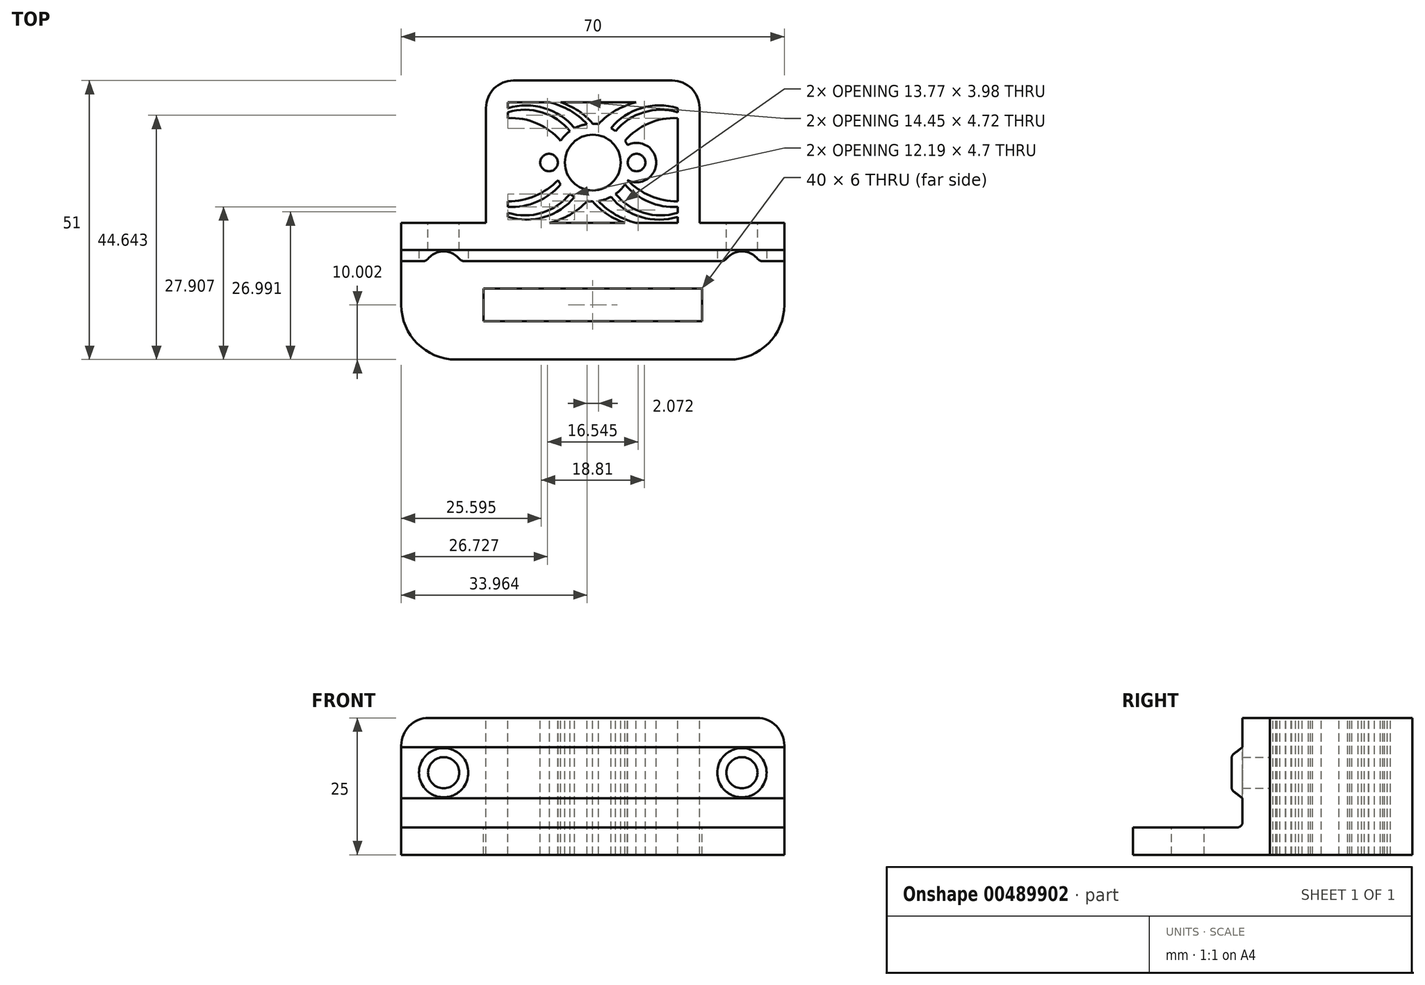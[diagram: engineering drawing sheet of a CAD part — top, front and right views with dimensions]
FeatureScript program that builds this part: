
annotation { "Feature Type Name" : "Feature", "Feature Type Description" : "" }
export const myFeature = defineFeature(function(context is Context, id is Id, definition is map)
    precondition{}
    {
        {
            var Q0;
            Q0=qCreatedBy(makeId("Top.planeOp"),FACE);
            var sketch = newSketch(context, id + "F0", { "sketchPlane" : qUnion([Q0])});
            skLineSegment(sketch, "E0.top", {"start": v(-40, -29.63) * mm, "end": v(0, -29.63) * mm});
            skLineSegment(sketch, "E0.left", {"start": v(-40, 0) * mm, "end": v(-40, -29.63) * mm});
            skLineSegment(sketch, "E0.right", {"start": v(0, 0) * mm, "end": v(0, -29.63) * mm});
            skPoint(sketch, "E1.oppositeSnap0", {"position": v(-20, -29.63) * mm});
            skLineSegment(sketch, "E2", {"start": v(-40, -9.63) * mm, "end": v(0, -9.63) * mm});
            skLineSegment(sketch, "E3", {"start": v(-20, -29.63) * mm, "end": v(-20, -9.63) * mm, "construction": true});
            skLineSegment(sketch, "E4.bottom", {"start": v(-55, -9.63) * mm, "end": v(15, -9.63) * mm});
            skLineSegment(sketch, "E4.top", {"start": v(-55, -4.63) * mm, "end": v(15, -4.63) * mm});
            skLineSegment(sketch, "E4.left", {"start": v(-55, -9.63) * mm, "end": v(-55, -4.63) * mm});
            skLineSegment(sketch, "E4.right", {"start": v(15, -9.63) * mm, "end": v(15, -4.63) * mm});
            skLineSegment(sketch, "E5", {"start": v(-55, -9.63) * mm, "end": v(-55, -19.63) * mm});
            skLineSegment(sketch, "E6", {"start": v(-45, -29.63) * mm, "end": v(-40, -29.63) * mm});
            skPoint(sketch, "E7.visualSharp", {"position": v(-55, -29.63) * mm});
            skArc(sketch, "E7.filletArc", {"start": v(-55, -19.63) * mm, "mid": v(-52.07, -26.7) * mm, "end": v(-45, -29.63) * mm});
            skLineSegment(sketch, "E8.MirrorCS", {"start": v(5, -29.63) * mm, "end": v(0, -29.63) * mm});
            skArc(sketch, "E9.MirrorCS", {"start": v(15, -19.63) * mm, "mid": v(12.07, -26.7) * mm, "end": v(5, -29.63) * mm});
            skLineSegment(sketch, "E10.MirrorCS", {"start": v(15, -9.63) * mm, "end": v(15, -19.63) * mm});
            skLineSegment(sketch, "E11.bottom", {"start": v(-40, -16.63) * mm, "end": v(0, -16.63) * mm});
            skLineSegment(sketch, "E11.top", {"start": v(-40, -22.63) * mm, "end": v(0, -22.63) * mm});
            skLineSegment(sketch, "E11.left", {"start": v(-40, -16.63) * mm, "end": v(-40, -22.63) * mm});
            skLineSegment(sketch, "E11.right", {"start": v(0, -16.63) * mm, "end": v(0, -22.63) * mm});
            skPoint(sketch, "E11.middle", {"position": v(-20, -19.63) * mm});
            skCircle(sketch, "E12", {"center": v(-20, 6.37) * mm, "radius": 5.1 * mm});
            skCircle(sketch, "E13", {"center": v(-28, 6.37) * mm, "radius": 1.6 * mm});
            skLineSegment(sketch, "E14", {"start": v(-20, 6.37) * mm, "end": v(-39.52, 6.37) * mm, "construction": true});
            skCircle(sketch, "E15.MirrorC", {"center": v(-12, 6.37) * mm, "radius": 1.6 * mm});
            skArc(sketch, "E16.0", {"start": v(-13.66, 9.57) * mm, "mid": v(-20, 13.47) * mm, "end": v(-26.34, 9.57) * mm});
            skArc(sketch, "E17.0", {"start": v(-26.34, 9.57) * mm, "mid": v(-31.6, 6.37) * mm, "end": v(-26.34, 3.18) * mm});
            skArc(sketch, "E18.0", {"start": v(-13.66, 9.57) * mm, "mid": v(-8.4, 6.37) * mm, "end": v(-13.66, 3.18) * mm});
            skArc(sketch, "E19.trimOffspring", {"start": v(-26.34, 3.18) * mm, "mid": v(-20, -0.73) * mm, "end": v(-13.66, 3.18) * mm});
            skLineSegment(sketch, "E20", {"start": v(-40, 0) * mm, "end": v(-40, 6.37) * mm});
            skLineSegment(sketch, "E21.MirrorCS", {"start": v(0, 0) * mm, "end": v(0, 6.37) * mm});
            skLineSegment(sketch, "E22.0", {"start": v(-35.5, -4.63) * mm, "end": v(-35.5, 17.37) * mm});
            skLineSegment(sketch, "E23.MirrorCS", {"start": v(-4.5, -4.63) * mm, "end": v(-4.5, 17.37) * mm});
            skLineSegment(sketch, "E24", {"start": v(-35.5, 17.37) * mm, "end": v(-4.5, 17.37) * mm});
            skArc(sketch, "E25", {"start": v(-18.95, 13.4) * mm, "mid": v(-15.82, 15.9) * mm, "end": v(-12.08, 17.37) * mm});
            skArc(sketch, "E26", {"start": v(-20, 13.47) * mm, "mid": v(-17.35, 15.83) * mm, "end": v(-14.15, 17.37) * mm});
            skArc(sketch, "E27.13.1", {"start": v(-14.11, 10.34) * mm, "mid": v(-9.8, 13.54) * mm, "end": v(-4.5, 14.48) * mm});
            skArc(sketch, "E27.14.0", {"start": v(-16.7, 12.65) * mm, "mid": v(-11.15, 16.33) * mm, "end": v(-4.5, 16.31) * mm});
            skArc(sketch, "E27.14.1", {"start": v(-13.66, 9.57) * mm, "mid": v(-9.48, 12.46) * mm, "end": v(-4.5, 13.48) * mm});
            skArc(sketch, "E27.15.0", {"start": v(-15.83, 12.12) * mm, "mid": v(-10.69, 15.57) * mm, "end": v(-4.5, 15.56) * mm});
            skPoint(sketch, "E28.trimOffspring.end.orphan", {"position": v(-6.09, 17.37) * mm});
            skLineSegment(sketch, "E29", {"start": v(-20, 6.37) * mm, "end": v(-20, -19.63) * mm, "construction": true});
            skArc(sketch, "E30.MirrorCS", {"start": v(-20, 13.47) * mm, "mid": v(-22.65, 15.83) * mm, "end": v(-25.85, 17.37) * mm});
            skArc(sketch, "E31.MirrorCS", {"start": v(-21.05, 13.4) * mm, "mid": v(-24.18, 15.9) * mm, "end": v(-27.92, 17.37) * mm});
            skArc(sketch, "E32.MirrorCS", {"start": v(-23.3, 12.65) * mm, "mid": v(-28.85, 16.33) * mm, "end": v(-35.5, 16.31) * mm});
            skArc(sketch, "E33.MirrorCS", {"start": v(-24.17, 12.12) * mm, "mid": v(-29.31, 15.57) * mm, "end": v(-35.5, 15.56) * mm});
            skArc(sketch, "E34.MirrorCS", {"start": v(-25.89, 10.34) * mm, "mid": v(-30.2, 13.54) * mm, "end": v(-35.5, 14.48) * mm});
            skArc(sketch, "E35.MirrorCS", {"start": v(-26.34, 9.57) * mm, "mid": v(-30.52, 12.46) * mm, "end": v(-35.5, 13.48) * mm});
            skArc(sketch, "E36.MirrorCS", {"start": v(-26.34, 3.18) * mm, "mid": v(-30.52, 0.28) * mm, "end": v(-35.5, -0.74) * mm});
            skArc(sketch, "E37.MirrorCS", {"start": v(-25.89, 2.4) * mm, "mid": v(-30.2, -0.8) * mm, "end": v(-35.5, -1.74) * mm});
            skArc(sketch, "E38.MirrorCS", {"start": v(-24.17, 0.63) * mm, "mid": v(-29.31, -2.82) * mm, "end": v(-35.5, -2.82) * mm});
            skArc(sketch, "E39.MirrorCS", {"start": v(-23.3, 0.1) * mm, "mid": v(-28.85, -3.59) * mm, "end": v(-35.5, -3.57) * mm});
            skArc(sketch, "E40.MirrorCS", {"start": v(-21.05, -0.65) * mm, "mid": v(-24.18, -3.16) * mm, "end": v(-27.92, -4.63) * mm});
            skArc(sketch, "E41.MirrorCS", {"start": v(-20, -0.73) * mm, "mid": v(-22.65, -3.09) * mm, "end": v(-25.85, -4.63) * mm});
            skArc(sketch, "E42.MirrorCS", {"start": v(-20, -0.73) * mm, "mid": v(-17.35, -3.09) * mm, "end": v(-14.15, -4.63) * mm});
            skArc(sketch, "E43.MirrorCS", {"start": v(-18.95, -0.65) * mm, "mid": v(-15.82, -3.16) * mm, "end": v(-12.08, -4.63) * mm});
            skArc(sketch, "E44.MirrorCS", {"start": v(-16.7, 0.1) * mm, "mid": v(-11.15, -3.59) * mm, "end": v(-4.5, -3.57) * mm});
            skArc(sketch, "E45.MirrorCS", {"start": v(-15.83, 0.63) * mm, "mid": v(-10.69, -2.82) * mm, "end": v(-4.5, -2.82) * mm});
            skArc(sketch, "E46.MirrorCS", {"start": v(-14.11, 2.4) * mm, "mid": v(-9.8, -0.8) * mm, "end": v(-4.5, -1.74) * mm});
            skArc(sketch, "E47.MirrorCS", {"start": v(-13.66, 3.18) * mm, "mid": v(-9.48, 0.28) * mm, "end": v(-4.5, -0.74) * mm});
            skLineSegment(sketch, "E48.0", {"start": v(-0.5, -4.63) * mm, "end": v(-0.5, 16.37) * mm});
            skLineSegment(sketch, "E48.1", {"start": v(-34.5, 21.37) * mm, "end": v(-5.5, 21.37) * mm});
            skLineSegment(sketch, "E48.2", {"start": v(-39.5, -4.63) * mm, "end": v(-39.5, 16.37) * mm});
            skPoint(sketch, "E49.visualSharp", {"position": v(-39.5, 21.37) * mm});
            skArc(sketch, "E49.filletArc", {"start": v(-34.5, 21.37) * mm, "mid": v(-38.04, 19.9) * mm, "end": v(-39.5, 16.37) * mm});
            skPoint(sketch, "E50.visualSharp", {"position": v(-0.5, 21.37) * mm});
            skArc(sketch, "E50.filletArc", {"start": v(-0.5, 16.37) * mm, "mid": v(-1.96, 19.9) * mm, "end": v(-5.5, 21.37) * mm});
            skSolve(sketch);
        }
        {
            var Q0;
            {var subQ5=sQuery(id+"F0.wireOp",EDGE,"E4.left");Q0=makeQuery(id+"F0.imprint","IMPRINT",FACE,{"disambiguationData":[TD([[makeQuery(id+"F0.imprint","IMPRINT",EDGE,{"derivedFrom":subQ5}),-1.0]])]});}
            var Q1;
            {var subQ5=sQuery(id+"F0.wireOp",EDGE,"E4.right");Q1=makeQuery(id+"F0.imprint","IMPRINT",FACE,{"disambiguationData":[TD([[makeQuery(id+"F0.imprint","IMPRINT",EDGE,{"derivedFrom":subQ5}),1.0]])]});}
            var Q2;
            {var subQ0=sQuery(id+"F0.wireOp",EDGE,"E0.top");Q2=makeQuery(id+"F0.imprint","IMPRINT",FACE,{"disambiguationData":[TD([[makeQuery(id+"F0.imprint","IMPRINT",EDGE,{"derivedFrom":subQ0}),1.0]])]});}
            var Q3;
            {var subQ2=sQuery(id+"F0.wireOp",EDGE,"E27.13.1");Q3=makeQuery(id+"F0.imprint","IMPRINT",FACE,{"disambiguationData":[TD([[makeQuery(id+"F0.imprint","IMPRINT",EDGE,{"derivedFrom":subQ2}),-1.0]])]});}
            var Q4;
            {var subQ0=sQuery(id+"F0.wireOp",EDGE,"E27.14.0");Q4=makeQuery(id+"F0.imprint","IMPRINT",FACE,{"disambiguationData":[TD([[makeQuery(id+"F0.imprint","IMPRINT",EDGE,{"derivedFrom":subQ0}),-1.0]])]});}
            var Q5;
            {var subQ0=sQuery(id+"F0.wireOp",EDGE,"E25");Q5=makeQuery(id+"F0.imprint","IMPRINT",FACE,{"disambiguationData":[TD([[makeQuery(id+"F0.imprint","IMPRINT",EDGE,{"derivedFrom":subQ0}),1.0]])]});}
            var Q6;
            {var subQ0=sQuery(id+"F0.wireOp",EDGE,"E30.MirrorCS");Q6=makeQuery(id+"F0.imprint","IMPRINT",FACE,{"disambiguationData":[TD([[makeQuery(id+"F0.imprint","IMPRINT",EDGE,{"derivedFrom":subQ0}),1.0]])]});}
            var Q7;
            {var subQ0=sQuery(id+"F0.wireOp",EDGE,"E32.MirrorCS");Q7=makeQuery(id+"F0.imprint","IMPRINT",FACE,{"disambiguationData":[TD([[makeQuery(id+"F0.imprint","IMPRINT",EDGE,{"derivedFrom":subQ0}),1.0]])]});}
            var Q8;
            {var subQ2=sQuery(id+"F0.wireOp",EDGE,"E34.MirrorCS");Q8=makeQuery(id+"F0.imprint","IMPRINT",FACE,{"disambiguationData":[TD([[makeQuery(id+"F0.imprint","IMPRINT",EDGE,{"derivedFrom":subQ2}),1.0]])]});}
            var Q9;
            {var subQ0=sQuery(id+"F0.wireOp",EDGE,"E36.MirrorCS");Q9=makeQuery(id+"F0.imprint","IMPRINT",FACE,{"disambiguationData":[TD([[makeQuery(id+"F0.imprint","IMPRINT",EDGE,{"derivedFrom":subQ0}),1.0]])]});}
            var Q10;
            {var subQ0=sQuery(id+"F0.wireOp",EDGE,"E38.MirrorCS");Q10=makeQuery(id+"F0.imprint","IMPRINT",FACE,{"disambiguationData":[TD([[makeQuery(id+"F0.imprint","IMPRINT",EDGE,{"derivedFrom":subQ0}),1.0]])]});}
            var Q11;
            {var subQ0=sQuery(id+"F0.wireOp",EDGE,"E44.MirrorCS");Q11=makeQuery(id+"F0.imprint","IMPRINT",FACE,{"disambiguationData":[TD([[makeQuery(id+"F0.imprint","IMPRINT",EDGE,{"derivedFrom":subQ0}),1.0]])]});}
            var Q12;
            {var subQ2=sQuery(id+"F0.wireOp",EDGE,"E46.MirrorCS");Q12=makeQuery(id+"F0.imprint","IMPRINT",FACE,{"disambiguationData":[TD([[makeQuery(id+"F0.imprint","IMPRINT",EDGE,{"derivedFrom":subQ2}),1.0]])]});}
            var Q13;
            {var subQ0=sQuery(id+"F0.wireOp",EDGE,"E5");Q13=makeQuery(id+"F0.imprint","IMPRINT",FACE,{"disambiguationData":[TD([[makeQuery(id+"F0.imprint","IMPRINT",EDGE,{"derivedFrom":subQ0}),1.0]])]});}
            var Q14;
            {var subQ0=sQuery(id+"F0.wireOp",EDGE,"E8.MirrorCS");Q14=makeQuery(id+"F0.imprint","IMPRINT",FACE,{"disambiguationData":[TD([[makeQuery(id+"F0.imprint","IMPRINT",EDGE,{"derivedFrom":subQ0}),-1.0]])]});}
            var Q15;
            {var subQ1=sQuery(id+"F0.wireOp",EDGE,"E0.left");var subQ5=sQuery(id+"F0.wireOp",EDGE,"E4.top");var subQ10=makeQuery(id+"F0.imprint","INTERSECT",VERTEX,{"derivedFrom":[subQ1,subQ5]});Q15=makeQuery(id+"F0.imprint","IMPRINT",FACE,{"disambiguationData":[TD([[makeQuery(id+"F0.imprint","IMPRINT",EDGE,{"disambiguationData":[TD([[subQ10,-1.0]])],"derivedFrom":subQ1}),1.0]])]});}
            var Q16;
            Q16=makeQuery(id+"F0.imprint","IMPRINT",FACE,{"disambiguationData":[TD([[makeQuery(id+"F0.imprint","IMPRINT",EDGE,{"derivedFrom":sQuery(id+"F0.wireOp",EDGE,"E12")}),-1.0]])]});
            var Q17;
            {var subQ0=sQuery(id+"F0.wireOp",EDGE,"E42.MirrorCS");Q17=makeQuery(id+"F0.imprint","IMPRINT",FACE,{"disambiguationData":[TD([[makeQuery(id+"F0.imprint","IMPRINT",EDGE,{"derivedFrom":subQ0}),1.0]])]});}
            var Q18;
            {var subQ0=sQuery(id+"F0.wireOp",EDGE,"E40.MirrorCS");Q18=makeQuery(id+"F0.imprint","IMPRINT",FACE,{"disambiguationData":[TD([[makeQuery(id+"F0.imprint","IMPRINT",EDGE,{"derivedFrom":subQ0}),1.0]])]});}
            var Q19;
            {var subQ24=sQuery(id+"F0.wireOp",EDGE,"E48.0");Q19=makeQuery(id+"F0.imprint","IMPRINT",FACE,{"disambiguationData":[TD([[makeQuery(id+"F0.imprint","IMPRINT",EDGE,{"derivedFrom":subQ24}),1.0]])]});}
            var Q20;
            {var subQ0=sQuery(id+"F0.wireOp",EDGE,"E11.bottom");Q20=makeQuery(id+"F0.imprint","IMPRINT",FACE,{"disambiguationData":[TD([[makeQuery(id+"F0.imprint","IMPRINT",EDGE,{"derivedFrom":subQ0}),1.0]])]});}
            extrude(context, id + "F1", {"entities" : qUnion([Q0, Q1, Q2, Q3, Q4, Q5, Q6, Q7, Q8, Q9, Q10, Q11, Q12, Q13, Q14, Q15, Q16, Q17, Q18, Q19, Q20]), "oppositeDirection" : true, "depth" : 25 * mm});
        }
        {
            var Q0;
            {var subQ1=sQuery(id+"F0.wireOp",EDGE,"E0.top");Q0=makeQuery(id+"F0.imprint","IMPRINT",FACE,{"disambiguationData":[TD([[makeQuery(id+"F0.imprint","IMPRINT",EDGE,{"derivedFrom":subQ1}),1.0]])]});}
            var Q1;
            {var subQ0=sQuery(id+"F0.wireOp",EDGE,"MP0E4fPa-GQLl-2h6X-QoBP-9llfqrqqr4Ud");Q1=makeQuery(id+"F0.imprint","IMPRINT",FACE,{"disambiguationData":[TD([[makeQuery(id+"F0.imprint","IMPRINT",EDGE,{"derivedFrom":subQ0}),-1.0]])]});}
            var Q2;
            {var subQ0=sQuery(id+"F0.wireOp",EDGE,"nStD9vQv-VlbH-pENE-0mBm-z8rxFK4uViPM");Q2=makeQuery(id+"F0.imprint","IMPRINT",FACE,{"disambiguationData":[TD([[makeQuery(id+"F0.imprint","IMPRINT",EDGE,{"derivedFrom":subQ0}),1.0]])]});}
            var Q3;
            {var subQ1=sQuery(id+"F0.wireOp",EDGE,"E5");Q3=makeQuery(id+"F0.imprint","IMPRINT",FACE,{"disambiguationData":[TD([[makeQuery(id+"F0.imprint","IMPRINT",EDGE,{"derivedFrom":subQ1}),1.0]])]});}
            var Q4;
            {var subQ0=sQuery(id+"F0.wireOp",EDGE,"E8.MirrorCS");Q4=makeQuery(id+"F0.imprint","IMPRINT",FACE,{"disambiguationData":[TD([[makeQuery(id+"F0.imprint","IMPRINT",EDGE,{"derivedFrom":subQ0}),-1.0]])]});}
            var Q5;
            {var subQ0=sQuery(id+"F0.wireOp",EDGE,"E11.bottom");Q5=makeQuery(id+"F0.imprint","IMPRINT",FACE,{"disambiguationData":[TD([[makeQuery(id+"F0.imprint","IMPRINT",EDGE,{"derivedFrom":subQ0}),1.0]])]});}
            extrude(context, id + "F2", {"entities" : qUnion([Q0, Q1, Q2, Q3, Q4, Q5]), "operationType" : NewBodyOperationType.REMOVE, "oppositeDirection" : true, "depth" : 20 * mm});
        }
        {
            var Q0;
            {var subQ0=sQuery(id+"F0.wireOp",EDGE,"E4.top");Q0=makeQuery(id+"F1.opExtrude","SWEPT_FACE",FACE,{"disambiguationData":[OSD([subQ0]),TDD([makeQuery(id+"F0.imprint","IMPRINT",EDGE,{"disambiguationData":[TD([[makeQuery(id+"F0.imprint","INTERSECT",VERTEX,{"derivedFrom":[subQ0,sQuery(id+"F0.wireOp",EDGE,"E4.left")]}),-1.0]])],"derivedFrom":subQ0})])]});}
            var sketch = newSketch(context, id + "F3", { "sketchPlane" : qUnion([Q0])});
            skCircle(sketch, "E51", {"center": v(47.25, -10) * mm, "radius": 2.85 * mm});
            skPoint(sketch, "E51.centerSnap0", {"position": v(47.25, 0) * mm});
            skPoint(sketch, "E51.centerSnap1", {"position": v(58, -10) * mm});
            skPoint(sketch, "E52.0", {"position": v(20, 0) * mm});
            skLineSegment(sketch, "E53", {"start": v(20, 0) * mm, "end": v(20, -39.52) * mm, "construction": true});
            skCircle(sketch, "E54.MirrorC", {"center": v(-7.25, -10) * mm, "radius": 2.85 * mm});
            skSolve(sketch);
        }
        {
            var Q0;
            Q0=makeQuery(id+"F1.opExtrude","SWEPT_FACE",FACE,{"disambiguationData":[OSD([sQuery(id+"F0.wireOp",EDGE,"E4.right"),sQuery(id+"F0.wireOp",EDGE,"E10.MirrorCS")])]});
            var sketch = newSketch(context, id + "F4", { "sketchPlane" : qUnion([Q0])});
            skLineSegment(sketch, "E55", {"start": v(-9.63, -10) * mm, "end": v(-13.18, -10) * mm, "construction": true});
            skLineSegment(sketch, "E56", {"start": v(-11.63, -10) * mm, "end": v(-11.63, -7.35) * mm});
            skLineSegment(sketch, "E57", {"start": v(-11.23, -6.55) * mm, "end": v(-9.63, -5.35) * mm});
            skLineSegment(sketch, "E58", {"start": v(-9.63, -5.35) * mm, "end": v(-9.63, -10) * mm});
            skPoint(sketch, "E59.visualSharp", {"position": v(-11.63, -6.85) * mm});
            skArc(sketch, "E59.filletArc", {"start": v(-11.23, -6.55) * mm, "mid": v(-11.52, -6.9) * mm, "end": v(-11.63, -7.35) * mm});
            skLineSegment(sketch, "E60.MirrorCS", {"start": v(-11.63, -10) * mm, "end": v(-11.63, -12.65) * mm});
            skArc(sketch, "E61.MirrorCS", {"start": v(-11.23, -13.45) * mm, "mid": v(-11.52, -13.1) * mm, "end": v(-11.63, -12.65) * mm});
            skLineSegment(sketch, "E62.MirrorCS", {"start": v(-11.23, -13.45) * mm, "end": v(-9.63, -14.65) * mm});
            skLineSegment(sketch, "E63.MirrorCS", {"start": v(-9.63, -14.65) * mm, "end": v(-9.63, -10) * mm});
            skSolve(sketch);
        }
        {
            var Q0;
            Q0=makeQuery(id+"F4.imprint","IMPRINT",FACE,{"disambiguationData":[TD([[makeQuery(id+"F4.imprint","IMPRINT",EDGE,{"derivedFrom":sQuery(id+"F4.wireOp",EDGE,"E56")}),-1.0]])]});
            var Q1;
            Q1=makeQuery(id+"F1.opExtrude","SWEPT_FACE",FACE,{"disambiguationData":[OSD([sQuery(id+"F0.wireOp",EDGE,"E4.left"),sQuery(id+"F0.wireOp",EDGE,"E5")])]});
            extrude(context, id + "F5", {"entities" : qUnion([Q0]), "operationType" : NewBodyOperationType.ADD, "endBound" : BoundingType.UP_TO_SURFACE, "oppositeDirection" : true, "endBoundEntityFace" : qUnion([Q1]), "depth" : 25 * mm});
        }
        {
            var Q0;
            Q0 = qSketchRegion(id + "F3", true);
            extrude(context, id + "F6", {"entities" : qUnion([Q0]), "operationType" : NewBodyOperationType.REMOVE, "endBound" : BoundingType.THROUGH_ALL, "oppositeDirection" : true, "depth" : 25 * mm});
        }
        {
            var Q0;
            Q0=makeQuery(id+"F6.boolean.opBoolean","SPLIT",FACE,{"disambiguationData":[TD([makeQuery(id+"F5.opExtrude","SWEPT_FACE",FACE,{"disambiguationData":[OSD([sQuery(id+"F4.wireOp",EDGE,"E59.filletArc")])]}),makeQuery(id+"F5.opExtrude","SWEPT_FACE",FACE,{"disambiguationData":[OSD([sQuery(id+"F4.wireOp",EDGE,"E61.MirrorCS")])]}),makeQuery(id+"F6.opExtrude","SWEPT_FACE",FACE,{"disambiguationData":[OSD([sQuery(id+"F3.wireOp",EDGE,"E51")])]}),makeQuery(id+"F6.opExtrude","SWEPT_FACE",FACE,{"disambiguationData":[OSD([sQuery(id+"F3.wireOp",EDGE,"E54.MirrorC")])]})])],"derivedFrom":makeQuery(id+"F5.opExtrude","SWEPT_FACE",FACE,{"disambiguationData":[OSD([sQuery(id+"F4.wireOp",EDGE,"E56"),sQuery(id+"F4.wireOp",EDGE,"E60.MirrorCS")])]})});
            var sketch = newSketch(context, id + "F7", { "sketchPlane" : qUnion([Q0])});
            skCircle(sketch, "E64.0", {"center": v(7.25, -10) * mm, "radius": 2.85 * mm});
            skCircle(sketch, "E65", {"center": v(7.25, -10) * mm, "radius": 4.5 * mm});
            skLineSegment(sketch, "E66", {"start": v(-20, -7.35) * mm, "end": v(-20, -14.58) * mm, "construction": true});
            skCircle(sketch, "E67.MirrorC", {"center": v(-47.25, -10) * mm, "radius": 4.5 * mm});
            skSolve(sketch);
        }
        {
            var Q0;
            Q0 = qSketchRegion(id + "F7", true);
            var Q1;
            {var subQ4=sQuery(id+"F4.wireOp",EDGE,"E57");Q1=makeQuery(id+"F5.boolean.opBoolean","SPLIT",FACE,{"disambiguationData":[TD([makeQuery(id+"F5.opExtrude","SWEPT_FACE",FACE,{"disambiguationData":[OSD([subQ4])]})])],"derivedFrom":makeQuery(id+"F2.boolean.opBoolean","COPY",FACE,{"derivedFrom":makeQuery(id+"F2.opExtrude","SWEPT_FACE",FACE,{"disambiguationData":[OSD([sQuery(id+"F0.wireOp",EDGE,"E4.bottom")])]})})});}
            extrude(context, id + "F8", {"entities" : qUnion([Q0]), "operationType" : NewBodyOperationType.REMOVE, "endBound" : BoundingType.UP_TO_SURFACE, "oppositeDirection" : true, "endBoundEntityFace" : qUnion([Q1]), "depth" : 25 * mm});
        }
        {
            var Q0;
            Q0=makeQuery(id+"F1.opExtrude","CAP_EDGE",EDGE,{"disambiguationData":[OSD([sQuery(id+"F0.wireOp",EDGE,"E4.right"),sQuery(id+"F0.wireOp",EDGE,"E10.MirrorCS")])],"isStart":true});
            var Q1;
            Q1=makeQuery(id+"F1.opExtrude","CAP_EDGE",EDGE,{"disambiguationData":[OSD([sQuery(id+"F0.wireOp",EDGE,"E4.left"),sQuery(id+"F0.wireOp",EDGE,"E5")])],"isStart":true});
            fillet(context, id + "F9", {"entities" : qUnion([Q0, Q1]), "radius" : 5 * mm, "tangentPropagation" : true, "allowEdgeOverflow" : false});
        }
        {
            var Q0;
            Q0=makeQuery(id+"F2.boolean.opBoolean","COPY",EDGE,{"derivedFrom":makeQuery(id+"F2.opExtrude","CAP_EDGE",EDGE,{"disambiguationData":[OSD([sQuery(id+"F0.wireOp",EDGE,"E4.bottom")])],"isStart":false})});
            fillet(context, id + "F10", {"entities" : qUnion([Q0]), "radius" : 1 * mm, "tangentPropagation" : true, "allowEdgeOverflow" : false});
        }
    });
